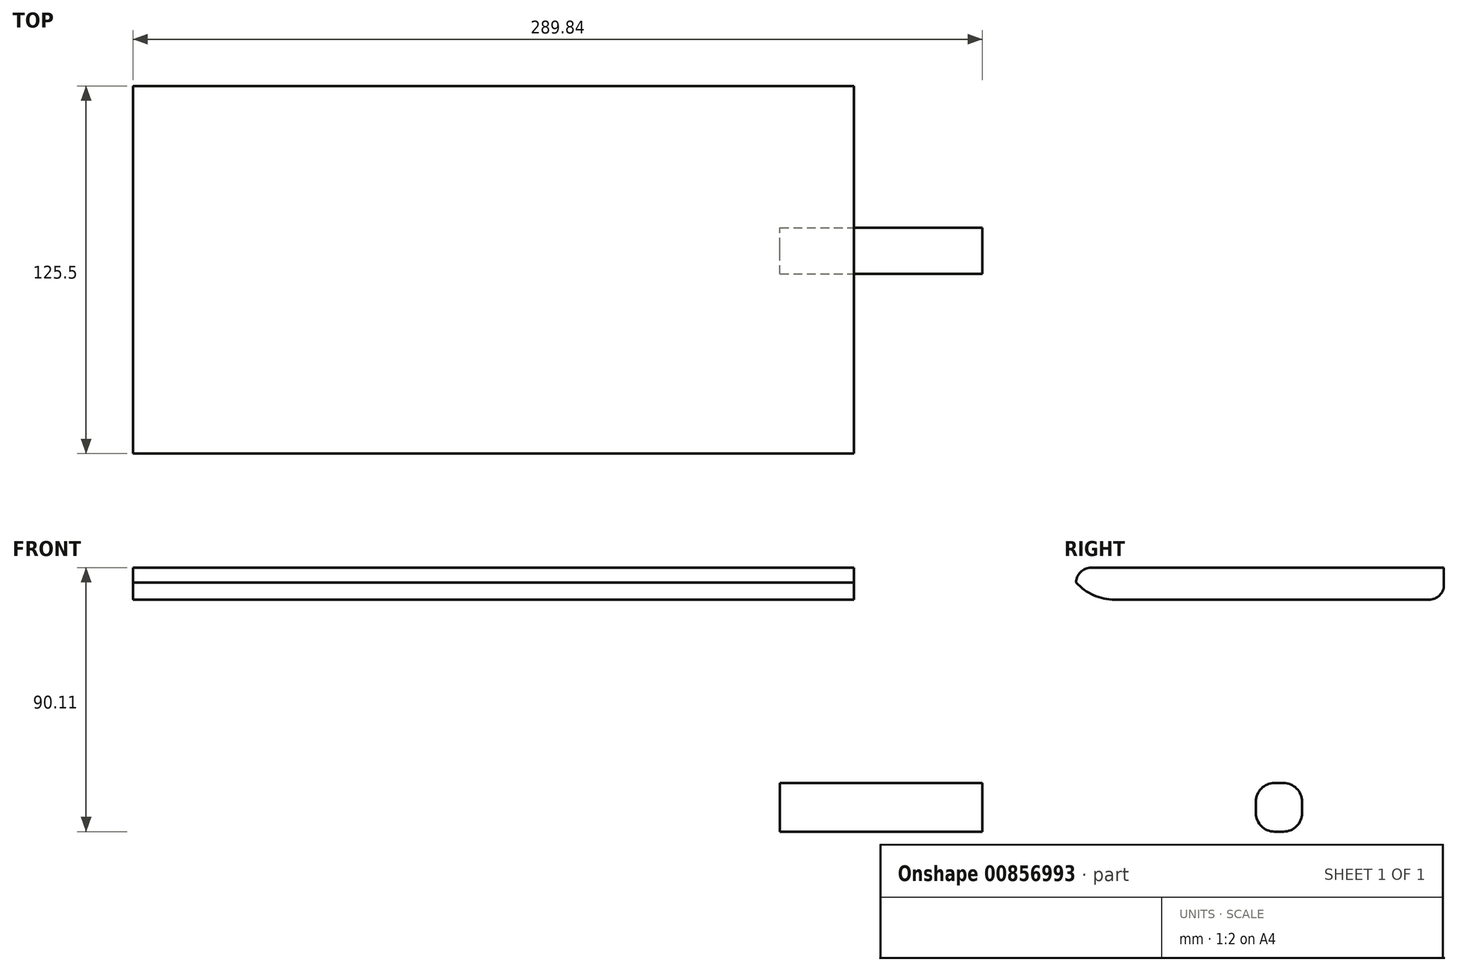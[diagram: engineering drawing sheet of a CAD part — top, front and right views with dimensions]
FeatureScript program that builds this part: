
annotation { "Feature Type Name" : "Feature", "Feature Type Description" : "" }
export const myFeature = defineFeature(function(context is Context, id is Id, definition is map)
    precondition{}
    {
        {
            var Q0;
            Q0=qCreatedBy(makeId("Top.planeOp"),FACE);
            var sketch = newSketch(context, id + "F0", { "sketchPlane" : qUnion([Q0])});
            skLineSegment(sketch, "E0.bottom", {"start": v(-113.37, 48.43) * mm, "end": v(132.58, 48.43) * mm});
            skLineSegment(sketch, "E0.top", {"start": v(-113.37, -77.07) * mm, "end": v(132.58, -77.07) * mm});
            skLineSegment(sketch, "E0.left", {"start": v(-113.37, 48.43) * mm, "end": v(-113.37, -77.07) * mm});
            skLineSegment(sketch, "E0.right", {"start": v(132.58, 48.43) * mm, "end": v(132.58, -77.07) * mm});
            skSolve(sketch);
        }
        {
            var Q0;
            Q0 = qSketchRegion(id + "F0", true);
            extrude(context, id + "F1", {"entities" : qUnion([Q0]), "depth" : 10.92 * mm, "offsetDistance" : 25.4 * mm});
        }
        {
            var Q0;
            Q0=makeQuery(id+"F1.opExtrude","CAP_EDGE",EDGE,{"disambiguationData":[OSD([sQuery(id+"F0.wireOp",EDGE,"E0.top")])],"isStart":false});
            fillet(context, id + "F2", {"entities" : qUnion([Q0]), "radius" : 5.08 * mm, "tangentPropagation" : true, "allowEdgeOverflow" : false});
        }
        {
            var Q0;
            Q0=makeQuery(id+"F1.opExtrude","CAP_EDGE",EDGE,{"disambiguationData":[OSD([sQuery(id+"F0.wireOp",EDGE,"E0.top")])],"isStart":true});
            fillet(context, id + "F3", {"entities" : qUnion([Q0]), "radius" : 17.78 * mm, "tangentPropagation" : true, "allowEdgeOverflow" : false});
        }
        {
            var Q0;
            Q0=makeQuery(id+"F1.opExtrude","CAP_EDGE",EDGE,{"disambiguationData":[OSD([sQuery(id+"F0.wireOp",EDGE,"E0.bottom")])],"isStart":true});
            fillet(context, id + "F4", {"entities" : qUnion([Q0]), "radius" : 5.08 * mm, "tangentPropagation" : true, "allowEdgeOverflow" : false});
        }
        {
            var Q0;
            Q0=qCreatedBy(makeId("Front.planeOp"),FACE);
            var sketch = newSketch(context, id + "F5", { "sketchPlane" : qUnion([Q0])});
            skLineSegment(sketch, "E1.bottom", {"start": v(107.4, -79.19) * mm, "end": v(176.47, -79.19) * mm});
            skLineSegment(sketch, "E1.top", {"start": v(107.4, -62.61) * mm, "end": v(176.47, -62.61) * mm});
            skLineSegment(sketch, "E1.left", {"start": v(107.4, -79.19) * mm, "end": v(107.4, -62.61) * mm});
            skLineSegment(sketch, "E1.right", {"start": v(176.47, -79.19) * mm, "end": v(176.47, -62.61) * mm});
            skSolve(sketch);
        }
        {
            var Q0;
            Q0 = qSketchRegion(id + "F5", true);
            extrude(context, id + "F6", {"entities" : qUnion([Q0]), "depth" : 15.75 * mm, "offsetDistance" : 25.4 * mm});
        }
        {
            var Q0;
            Q0=makeQuery(id+"F6.opExtrude","CAP_EDGE",EDGE,{"disambiguationData":[OSD([sQuery(id+"F5.wireOp",EDGE,"E1.bottom")])],"isStart":true});
            fillet(context, id + "F7", {"entities" : qUnion([Q0]), "radius" : 6.35 * mm, "tangentPropagation" : true, "allowEdgeOverflow" : false});
        }
        {
            var Q0;
            Q0=makeQuery(id+"F6.opExtrude","CAP_EDGE",EDGE,{"disambiguationData":[OSD([sQuery(id+"F5.wireOp",EDGE,"E1.top")])],"isStart":true});
            fillet(context, id + "F8", {"entities" : qUnion([Q0]), "radius" : 6.35 * mm, "tangentPropagation" : true, "allowEdgeOverflow" : false});
        }
        {
            var Q0;
            Q0=makeQuery(id+"F6.opExtrude","CAP_EDGE",EDGE,{"disambiguationData":[OSD([sQuery(id+"F5.wireOp",EDGE,"E1.bottom")])],"isStart":false});
            fillet(context, id + "F9", {"entities" : qUnion([Q0]), "radius" : 6.35 * mm, "tangentPropagation" : true, "allowEdgeOverflow" : false});
        }
        {
            var Q0;
            Q0=makeQuery(id+"F6.opExtrude","CAP_EDGE",EDGE,{"disambiguationData":[OSD([sQuery(id+"F5.wireOp",EDGE,"E1.top")])],"isStart":false});
            fillet(context, id + "F10", {"entities" : qUnion([Q0]), "radius" : 6.35 * mm, "tangentPropagation" : true, "allowEdgeOverflow" : false});
        }
    });
